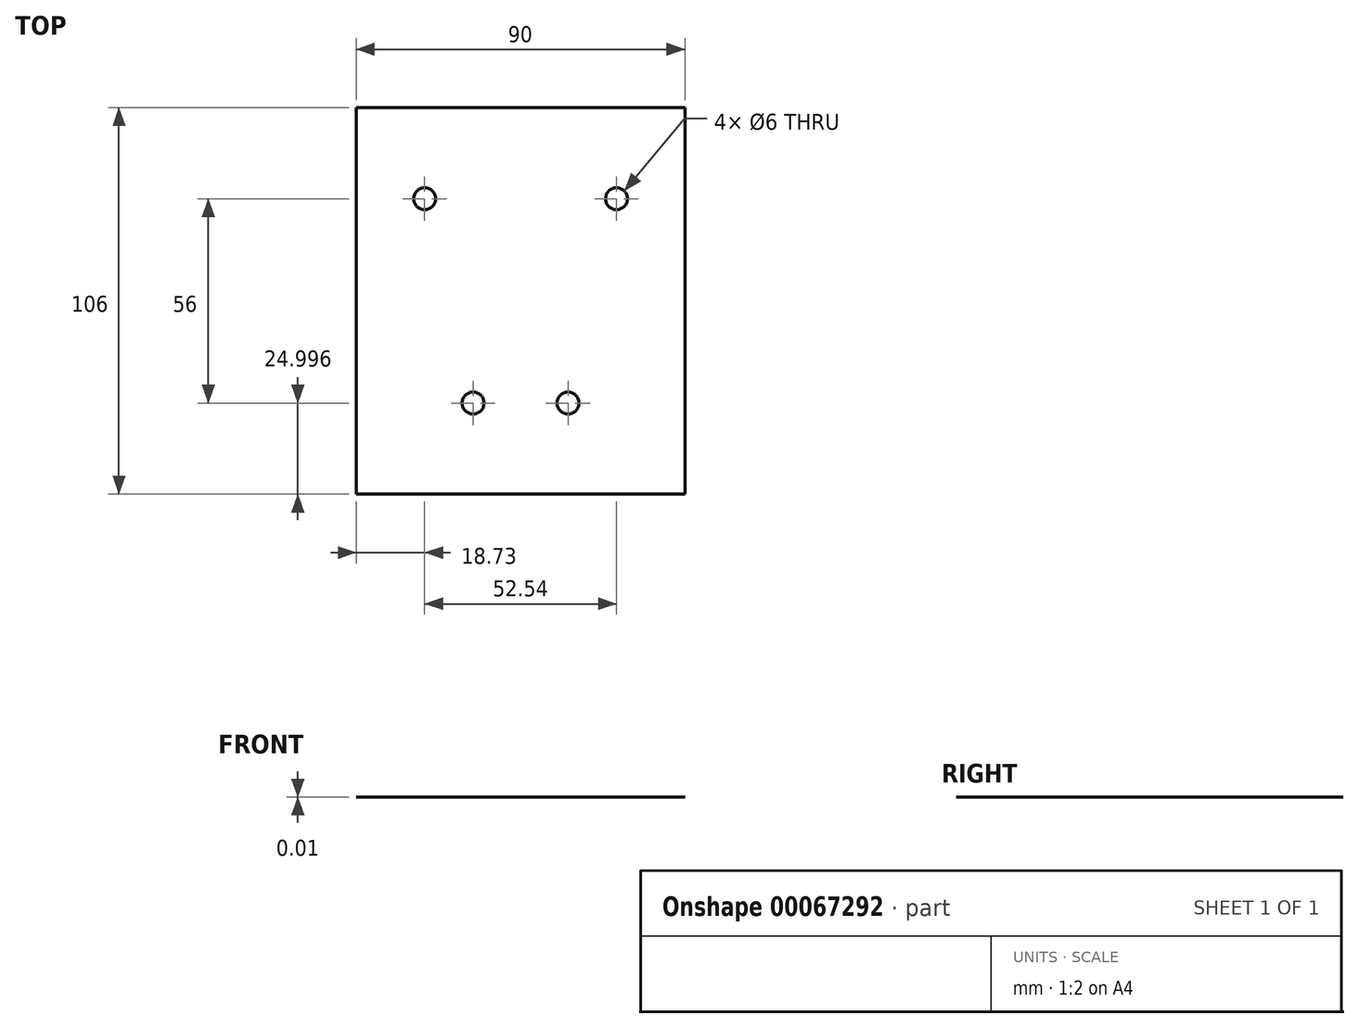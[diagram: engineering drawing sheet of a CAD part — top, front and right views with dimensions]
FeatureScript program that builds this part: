
annotation { "Feature Type Name" : "Feature", "Feature Type Description" : "" }
export const myFeature = defineFeature(function(context is Context, id is Id, definition is map)
    precondition{}
    {
        {
            var Q0;
            Q0=qCreatedBy(makeId("Top.planeOp"),FACE);
            var sketch = newSketch(context, id + "F0", { "sketchPlane" : qUnion([Q0])});
            skLineSegment(sketch, "E0.bottom", {"start": v(-41.78, 62.42) * mm, "end": v(48.22, 62.42) * mm});
            skLineSegment(sketch, "E0.top", {"start": v(-41.78, -43.58) * mm, "end": v(48.22, -43.58) * mm});
            skLineSegment(sketch, "E0.left", {"start": v(-41.78, 62.42) * mm, "end": v(-41.78, -43.58) * mm});
            skLineSegment(sketch, "E0.right", {"start": v(48.22, 62.42) * mm, "end": v(48.22, -43.58) * mm});
            skSolve(sketch);
        }
        {
            var Q0;
            Q0 = qSketchRegion(id + "F0", true);
            extrude(context, id + "F1", {"entities" : qUnion([Q0]), "depth" : 1 / 101.6 * mm});
        }
        {
            var Q0;
            Q0=makeQuery(id+"F1.opExtrude","CAP_FACE",FACE,{"disambiguationData":[OSD([sQuery(id+"F0.wireOp",EDGE,"E0.bottom"),sQuery(id+"F0.wireOp",EDGE,"E0.top"),sQuery(id+"F0.wireOp",EDGE,"E0.left"),sQuery(id+"F0.wireOp",EDGE,"E0.right")])],"isStart":false});
            var sketch = newSketch(context, id + "F2", { "sketchPlane" : qUnion([Q0])});
            skCircle(sketch, "E1", {"center": v(-23.05, 37.42) * mm, "radius": 3 * mm});
            skCircle(sketch, "E2", {"center": v(29.49, 37.42) * mm, "radius": 3 * mm});
            skCircle(sketch, "E3", {"center": v(-9.78, -18.58) * mm, "radius": 3 * mm});
            skCircle(sketch, "E4", {"center": v(16.22, -18.58) * mm, "radius": 3 * mm});
            skSolve(sketch);
        }
        {
            var Q0;
            Q0 = qSketchRegion(id + "F2", true);
            extrude(context, id + "F3", {"entities" : qUnion([Q0]), "operationType" : NewBodyOperationType.REMOVE, "oppositeDirection" : true, "depth" : 25 * mm});
        }
    });
